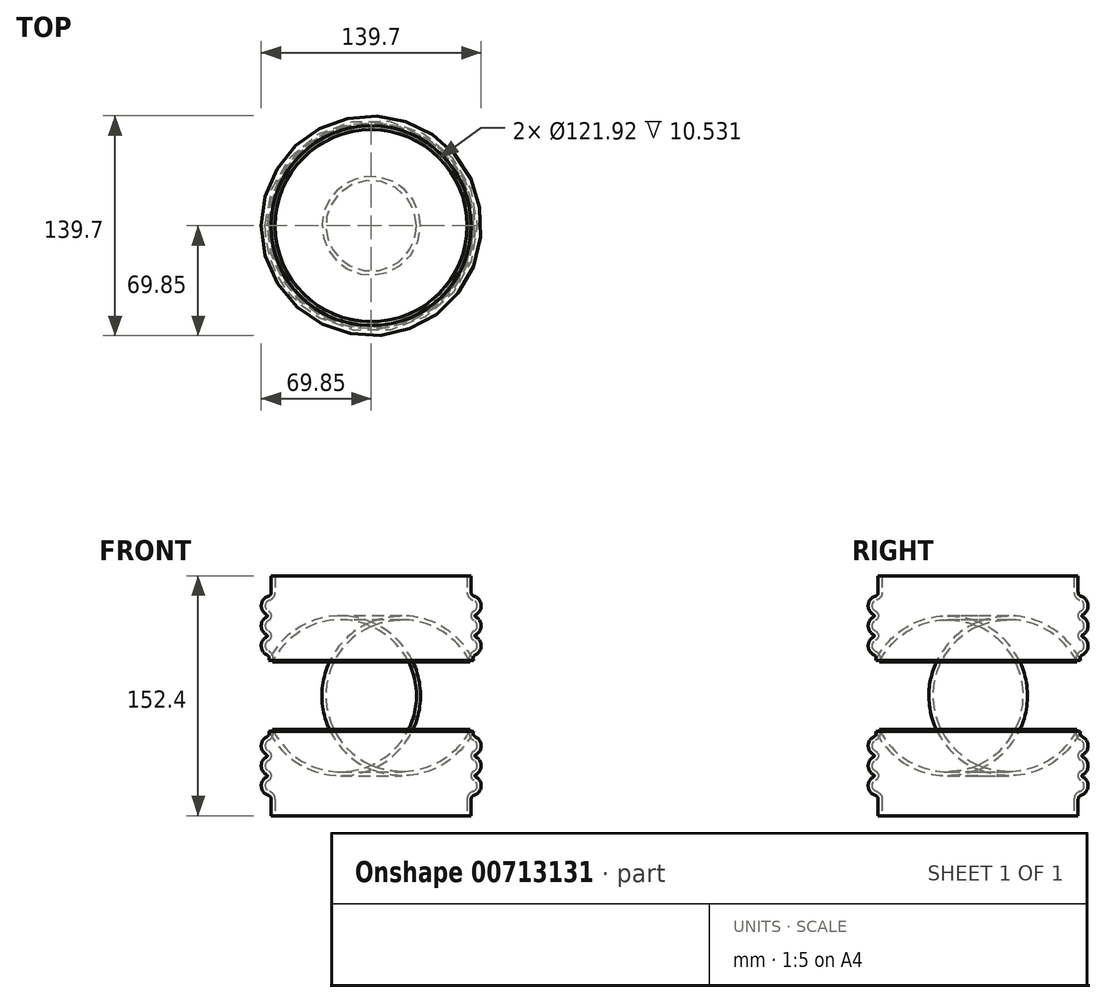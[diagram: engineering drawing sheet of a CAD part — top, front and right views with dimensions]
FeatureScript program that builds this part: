
annotation { "Feature Type Name" : "Feature", "Feature Type Description" : "" }
export const myFeature = defineFeature(function(context is Context, id is Id, definition is map)
    precondition{}
    {
        {
            var Q0;
            Q0=qCreatedBy(makeId("Front.planeOp"),FACE);
            var sketch = newSketch(context, id + "F0", { "sketchPlane" : qUnion([Q0])});
            skLineSegment(sketch, "E0", {"start": v(0, 0) * mm, "end": v(0, 76.2) * mm});
            skLineSegment(sketch, "E1", {"start": v(0, 76.2) * mm, "end": v(-114.16, 76.2) * mm, "construction": true});
            skLineSegment(sketch, "E2", {"start": v(0, 0) * mm, "end": v(-63.5, 0) * mm});
            skLineSegment(sketch, "E3", {"start": v(-63.5, 0) * mm, "end": v(-63.5, 10.53) * mm});
            skArc(sketch, "E4", {"start": v(-66.36, 24.72) * mm, "mid": v(-69.83, 18.49) * mm, "end": v(-65.31, 12.96) * mm});
            skArc(sketch, "E5.0.1.0", {"start": v(-66.36, 37.42) * mm, "mid": v(-69.85, 31.75) * mm, "end": v(-66.36, 26.08) * mm});
            skArc(sketch, "E5.0.2.0", {"start": v(-66.2, 50.2) * mm, "mid": v(-69.85, 44.54) * mm, "end": v(-66.36, 38.78) * mm});
            skLineSegment(sketch, "E5.direction1", {"start": v(-63.5, 12.7) * mm, "end": v(-38.1, 12.7) * mm, "construction": true});
            skLineSegment(sketch, "E5.direction2", {"start": v(-63.5, 12.7) * mm, "end": v(-63.5, 25.4) * mm, "construction": true});
            skArc(sketch, "E6", {"start": v(-70.3, 76.2) * mm, "mid": v(-68.96, 64.6) * mm, "end": v(-65.01, 53.62) * mm});
            skPoint(sketch, "E7.visualSharp", {"position": v(-63.5, 12.7) * mm});
            skArc(sketch, "E7.filletArc", {"start": v(-63.5, 10.53) * mm, "mid": v(-64, 12.05) * mm, "end": v(-65.31, 12.96) * mm});
            skPoint(sketch, "E8.visualSharp", {"position": v(-63.5, 25.4) * mm});
            skArc(sketch, "E8.filletArc", {"start": v(-66.36, 24.72) * mm, "mid": v(-65.94, 25.4) * mm, "end": v(-66.36, 26.08) * mm});
            skPoint(sketch, "E9.visualSharp", {"position": v(-63.5, 38.1) * mm});
            skArc(sketch, "E9.filletArc", {"start": v(-66.36, 37.42) * mm, "mid": v(-65.94, 38.1) * mm, "end": v(-66.36, 38.78) * mm});
            skPoint(sketch, "E10.visualSharp", {"position": v(-63.5, 50.8) * mm});
            skArc(sketch, "E10.filletArc", {"start": v(-66.2, 50.2) * mm, "mid": v(-64.89, 51.66) * mm, "end": v(-65.01, 53.62) * mm});
            skArc(sketch, "E11.MirrorCS", {"start": v(-63.5, 141.87) * mm, "mid": v(-64, 140.35) * mm, "end": v(-65.31, 139.44) * mm});
            skArc(sketch, "E12.MirrorCS", {"start": v(-66.2, 102.2) * mm, "mid": v(-64.89, 100.74) * mm, "end": v(-65.01, 98.78) * mm});
            skArc(sketch, "E13.MirrorCS", {"start": v(-66.36, 127.68) * mm, "mid": v(-65.94, 127) * mm, "end": v(-66.36, 126.32) * mm});
            skArc(sketch, "E14.MirrorCS", {"start": v(-66.36, 114.98) * mm, "mid": v(-65.94, 114.3) * mm, "end": v(-66.36, 113.62) * mm});
            skPoint(sketch, "E15.MirrorP", {"position": v(-63.5, 101.6) * mm});
            skLineSegment(sketch, "E16.MirrorCS", {"start": v(0, 152.4) * mm, "end": v(0, 76.2) * mm});
            skPoint(sketch, "E17.MirrorP", {"position": v(-63.5, 127) * mm});
            skArc(sketch, "E18.MirrorCS", {"start": v(-66.36, 127.68) * mm, "mid": v(-69.83, 133.91) * mm, "end": v(-65.31, 139.44) * mm});
            skLineSegment(sketch, "E19.MirrorCS", {"start": v(0, 152.4) * mm, "end": v(-63.5, 152.4) * mm});
            skPoint(sketch, "E20.MirrorP", {"position": v(-63.5, 114.3) * mm});
            skPoint(sketch, "E21.MirrorP", {"position": v(-63.5, 139.7) * mm});
            skLineSegment(sketch, "E22.MirrorCS", {"start": v(-63.5, 152.4) * mm, "end": v(-63.5, 141.87) * mm});
            skArc(sketch, "E23.MirrorCS", {"start": v(-66.36, 114.98) * mm, "mid": v(-69.85, 120.65) * mm, "end": v(-66.36, 126.32) * mm});
            skLineSegment(sketch, "E24.MirrorCS", {"start": v(-63.5, 139.7) * mm, "end": v(-38.1, 139.7) * mm, "construction": true});
            skLineSegment(sketch, "E25.MirrorCS", {"start": v(-63.5, 139.7) * mm, "end": v(-63.5, 127) * mm, "construction": true});
            skArc(sketch, "E26.MirrorCS", {"start": v(-70.3, 76.2) * mm, "mid": v(-68.96, 87.8) * mm, "end": v(-65.01, 98.78) * mm});
            skArc(sketch, "E27.MirrorCS", {"start": v(-66.2, 102.2) * mm, "mid": v(-69.85, 107.86) * mm, "end": v(-66.36, 113.62) * mm});
            skSolve(sketch);
        }
        {
            var Q0;
            Q0=makeQuery(id+"F0.imprint","IMPRINT",FACE,{"disambiguationData":[TD([[makeQuery(id+"F0.imprint","IMPRINT",EDGE,{"derivedFrom":sQuery(id+"F0.wireOp",EDGE,"E0")}),1.0]])]});
            var Q1;
            Q1=sQuery(id+"F0.wireOp",EDGE,"E0");
            revolve(context, id + "F1", {"surfaceOperationType" : NewSurfaceOperationType.NEW, "entities" : qUnion([Q0]), "axis" : qUnion([Q1]), "revolveType" : RevolveType.FULL});
        }
        {
            var Q0;
            Q0=makeQuery(id+"F1.opRevolve","SWEPT_FACE",FACE,{"disambiguationData":[OSD([sQuery(id+"F0.wireOp",EDGE,"E19.MirrorCS")])]});
            var Q1;
            Q1=makeQuery(id+"F1.opRevolve","SWEPT_FACE",FACE,{"disambiguationData":[OSD([sQuery(id+"F0.wireOp",EDGE,"E2")])]});
            shell(context, id + "F2", {"entities" : qUnion([Q0, Q1]), "thickness" : 2.54 * mm});
        }
    });
